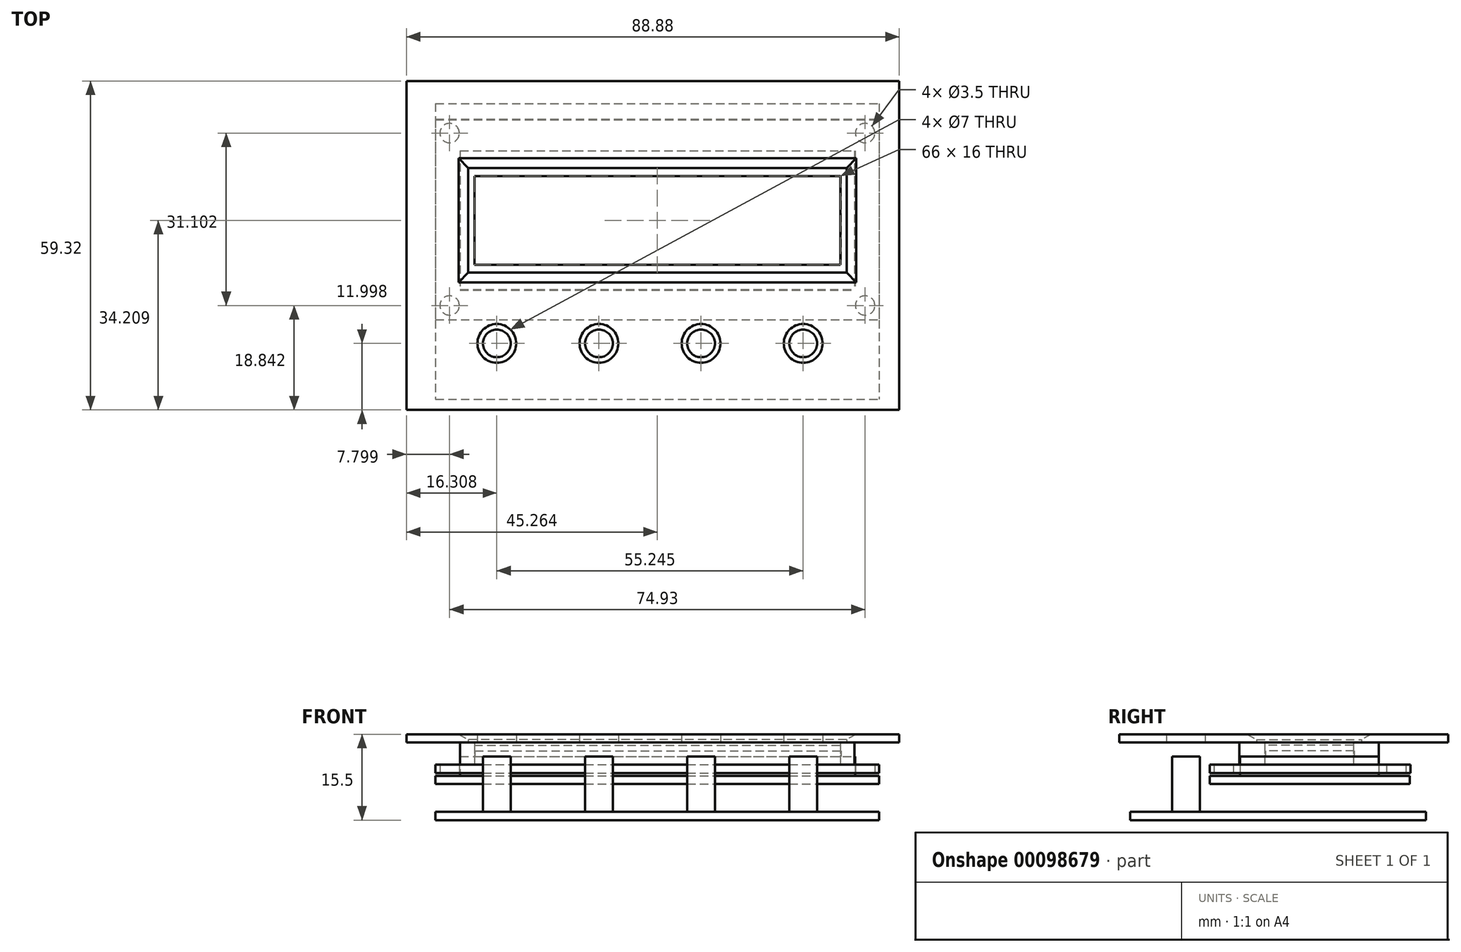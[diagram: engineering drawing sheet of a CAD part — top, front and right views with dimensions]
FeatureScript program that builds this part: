
annotation { "Feature Type Name" : "Feature", "Feature Type Description" : "" }
export const myFeature = defineFeature(function(context is Context, id is Id, definition is map)
    precondition{}
    {
        {
            var Q0;
            Q0=qCreatedBy(makeId("Top.planeOp"),FACE);
            var sketch = newSketch(context, id + "F0", { "sketchPlane" : qUnion([Q0])});
            skLineSegment(sketch, "E0.bottom", {"start": v(-57.33, 22.05) * mm, "end": v(22.68, 22.05) * mm});
            skLineSegment(sketch, "E0.top", {"start": v(-57.33, -31.29) * mm, "end": v(22.68, -31.29) * mm});
            skLineSegment(sketch, "E0.left", {"start": v(-57.33, 22.05) * mm, "end": v(-57.33, -31.29) * mm});
            skLineSegment(sketch, "E0.right", {"start": v(22.68, 22.05) * mm, "end": v(22.68, -31.29) * mm});
            skCircle(sketch, "E1", {"center": v(-46.28, -21.24) * mm, "radius": 2.5 * mm});
            skCircle(sketch, "E2", {"center": v(-27.87, -21.24) * mm, "radius": 2.5 * mm});
            skCircle(sketch, "E3", {"center": v(8.96, -21.24) * mm, "radius": 2.5 * mm});
            skCircle(sketch, "E4", {"center": v(-9.45, -21.24) * mm, "radius": 2.5 * mm});
            skLineSegment(sketch, "E5", {"start": v(-57.33, -16.94) * mm, "end": v(22.68, -16.94) * mm});
            skLineSegment(sketch, "E6", {"start": v(-57.33, 19.13) * mm, "end": v(22.68, 19.13) * mm});
            skLineSegment(sketch, "E7.bottom", {"start": v(-52.89, 13.54) * mm, "end": v(18.36, 13.54) * mm});
            skLineSegment(sketch, "E7.top", {"start": v(-52.89, -11.48) * mm, "end": v(18.36, -11.48) * mm});
            skLineSegment(sketch, "E7.left", {"start": v(-52.89, 13.54) * mm, "end": v(-52.89, -11.48) * mm});
            skLineSegment(sketch, "E7.right", {"start": v(18.36, 13.54) * mm, "end": v(18.36, -11.48) * mm});
            skLineSegment(sketch, "E8.bottom", {"start": v(-50.22, 9.1) * mm, "end": v(15.82, 9.1) * mm});
            skLineSegment(sketch, "E8.top", {"start": v(-50.22, -6.9) * mm, "end": v(15.82, -6.9) * mm});
            skLineSegment(sketch, "E8.left", {"start": v(-50.22, 9.1) * mm, "end": v(-50.22, -6.9) * mm});
            skLineSegment(sketch, "E8.right", {"start": v(15.82, 9.1) * mm, "end": v(15.82, -6.9) * mm});
            skSolve(sketch);
        }
        {
            var Q0;
            {var subQ1=sQuery(id+"F0.wireOp",EDGE,"E5");Q0=makeQuery(id+"F0.imprint","IMPRINT",FACE,{"disambiguationData":[TD([[makeQuery(id+"F0.imprint","IMPRINT",EDGE,{"derivedFrom":subQ1}),1.0]])]});}
            var Q1;
            Q1=makeQuery(id+"F0.imprint","IMPRINT",FACE,{"disambiguationData":[TD([[makeQuery(id+"F0.imprint","IMPRINT",EDGE,{"derivedFrom":sQuery(id+"F0.wireOp",EDGE,"E8.bottom")}),-1.0]])]});
            var Q2;
            {var subQ0=sQuery(id+"F0.wireOp",EDGE,"E0.bottom");Q2=makeQuery(id+"F0.imprint","IMPRINT",FACE,{"disambiguationData":[TD([[makeQuery(id+"F0.imprint","IMPRINT",EDGE,{"derivedFrom":subQ0}),-1.0]])]});}
            var Q3;
            Q3=makeQuery(id+"F0.imprint","IMPRINT",FACE,{"disambiguationData":[TD([[makeQuery(id+"F0.imprint","IMPRINT",EDGE,{"derivedFrom":sQuery(id+"F0.wireOp",EDGE,"E4")}),1.0]])]});
            var Q4;
            Q4=makeQuery(id+"F0.imprint","IMPRINT",FACE,{"disambiguationData":[TD([[makeQuery(id+"F0.imprint","IMPRINT",EDGE,{"derivedFrom":sQuery(id+"F0.wireOp",EDGE,"E7.bottom")}),-1.0]])]});
            var Q5;
            Q5=makeQuery(id+"F0.imprint","IMPRINT",FACE,{"disambiguationData":[TD([[makeQuery(id+"F0.imprint","IMPRINT",EDGE,{"derivedFrom":sQuery(id+"F0.wireOp",EDGE,"E1")}),1.0]])]});
            var Q6;
            Q6=makeQuery(id+"F0.imprint","IMPRINT",FACE,{"disambiguationData":[TD([[makeQuery(id+"F0.imprint","IMPRINT",EDGE,{"derivedFrom":sQuery(id+"F0.wireOp",EDGE,"E2")}),1.0]])]});
            var Q7;
            Q7=makeQuery(id+"F0.imprint","IMPRINT",FACE,{"disambiguationData":[TD([[makeQuery(id+"F0.imprint","IMPRINT",EDGE,{"derivedFrom":sQuery(id+"F0.wireOp",EDGE,"E3")}),1.0]])]});
            var Q8;
            {var subQ0=sQuery(id+"F0.wireOp",EDGE,"E0.top");Q8=makeQuery(id+"F0.imprint","IMPRINT",FACE,{"disambiguationData":[TD([[makeQuery(id+"F0.imprint","IMPRINT",EDGE,{"derivedFrom":subQ0}),1.0]])]});}
            extrude(context, id + "F1", {"entities" : qUnion([Q0, Q1, Q2, Q3, Q4, Q5, Q6, Q7, Q8]), "oppositeDirection" : true, "depth" : 1.5 * mm});
        }
        {
            var Q0;
            Q0=makeQuery(id+"F0.imprint","IMPRINT",FACE,{"disambiguationData":[TD([[makeQuery(id+"F0.imprint","IMPRINT",EDGE,{"derivedFrom":sQuery(id+"F0.wireOp",EDGE,"E1")}),1.0]])]});
            var Q1;
            Q1=makeQuery(id+"F0.imprint","IMPRINT",FACE,{"disambiguationData":[TD([[makeQuery(id+"F0.imprint","IMPRINT",EDGE,{"derivedFrom":sQuery(id+"F0.wireOp",EDGE,"E2")}),1.0]])]});
            var Q2;
            Q2=makeQuery(id+"F0.imprint","IMPRINT",FACE,{"disambiguationData":[TD([[makeQuery(id+"F0.imprint","IMPRINT",EDGE,{"derivedFrom":sQuery(id+"F0.wireOp",EDGE,"E4")}),1.0]])]});
            var Q3;
            Q3=makeQuery(id+"F0.imprint","IMPRINT",FACE,{"disambiguationData":[TD([[makeQuery(id+"F0.imprint","IMPRINT",EDGE,{"derivedFrom":sQuery(id+"F0.wireOp",EDGE,"E3")}),1.0]])]});
            extrude(context, id + "F2", {"entities" : qUnion([Q0, Q1, Q2, Q3]), "depth" : 10 * mm});
        }
        {
            var Q0;
            Q0=makeQuery(id+"F1.opExtrude","CAP_FACE",FACE,{"disambiguationData":[OSD([sQuery(id+"F0.wireOp",EDGE,"E0.bottom"),sQuery(id+"F0.wireOp",EDGE,"E0.top"),sQuery(id+"F0.wireOp",EDGE,"E0.left"),sQuery(id+"F0.wireOp",EDGE,"E0.right")])],"isStart":true});
            cPlane(context, id + "F3", {"entities" : qUnion([Q0]), "cplaneType" : CPlaneType.OFFSET, "offset" : 7 * mm, "width" : 150 * mm, "height" : 150 * mm});
        }
        {
            var Q0;
            Q0=qCreatedBy(id+"F3.planeOp",FACE);
            var sketch = newSketch(context, id + "F4", { "sketchPlane" : qUnion([Q0])});
            skLineSegment(sketch, "E9.0", {"start": v(-57.33, 22.05) * mm, "end": v(-57.33, -31.29) * mm, "construction": true});
            skLineSegment(sketch, "E10.0", {"start": v(-57.33, -31.29) * mm, "end": v(22.68, -31.29) * mm, "construction": true});
            skLineSegment(sketch, "E11.bottom", {"start": v(-57.33, 19.24) * mm, "end": v(22.68, 19.24) * mm});
            skLineSegment(sketch, "E11.top", {"start": v(-57.33, -16.94) * mm, "end": v(22.68, -16.94) * mm});
            skLineSegment(sketch, "E11.left", {"start": v(-57.33, 19.24) * mm, "end": v(-57.33, -16.94) * mm});
            skLineSegment(sketch, "E11.right", {"start": v(22.68, 19.24) * mm, "end": v(22.68, -16.94) * mm});
            skCircle(sketch, "E12", {"center": v(-54.8, -14.4) * mm, "radius": 1.75 * mm});
            skCircle(sketch, "E13", {"center": v(-54.8, 16.7) * mm, "radius": 1.75 * mm});
            skCircle(sketch, "E14", {"center": v(20.14, 16.7) * mm, "radius": 1.75 * mm});
            skCircle(sketch, "E15", {"center": v(20.14, -14.4) * mm, "radius": 1.75 * mm});
            skSolve(sketch);
        }
        {
            var Q0;
            Q0 = qSketchRegion(id + "F4", true);
            extrude(context, id + "F5", {"entities" : qUnion([Q0]), "depth" : 1.5 * mm});
        }
        {
            var Q0;
            Q0=makeQuery(id+"F5.opExtrude","CAP_FACE",FACE,{"disambiguationData":[OSD([sQuery(id+"F4.wireOp",EDGE,"E11.bottom"),sQuery(id+"F4.wireOp",EDGE,"E11.top"),sQuery(id+"F4.wireOp",EDGE,"E11.left"),sQuery(id+"F4.wireOp",EDGE,"E11.right"),sQuery(id+"F4.wireOp",EDGE,"E12"),sQuery(id+"F4.wireOp",EDGE,"E13"),sQuery(id+"F4.wireOp",EDGE,"E14"),sQuery(id+"F4.wireOp",EDGE,"E15"),sQuery(id+"F4.wireOp",EDGE,"9yUqGMXj-hSxB-kQKk-yNBa-DG6KZY831I2t")])],"isStart":false});
            var sketch = newSketch(context, id + "F6", { "sketchPlane" : qUnion([Q0])});
            skLineSegment(sketch, "E16.bottom", {"start": v(-52.89, 13.54) * mm, "end": v(18.23, 13.54) * mm});
            skLineSegment(sketch, "E16.top", {"start": v(-52.89, -11.6) * mm, "end": v(18.23, -11.6) * mm});
            skLineSegment(sketch, "E16.left", {"start": v(-52.89, 13.54) * mm, "end": v(-52.89, -11.6) * mm});
            skLineSegment(sketch, "E16.right", {"start": v(18.23, 13.54) * mm, "end": v(18.23, -11.6) * mm});
            skLineSegment(sketch, "E17.0", {"start": v(-57.33, 19.24) * mm, "end": v(22.68, 19.24) * mm});
            skLineSegment(sketch, "E18", {"start": v(-17.33, 19.24) * mm, "end": v(-17.33, -16.94) * mm, "construction": true});
            skLineSegment(sketch, "E19.bottom", {"start": v(-50.33, 8.97) * mm, "end": v(15.67, 8.97) * mm});
            skLineSegment(sketch, "E19.top", {"start": v(-50.33, -7.03) * mm, "end": v(15.67, -7.03) * mm});
            skLineSegment(sketch, "E19.left", {"start": v(-50.33, 8.97) * mm, "end": v(-50.33, -7.03) * mm});
            skLineSegment(sketch, "E19.right", {"start": v(15.67, 8.97) * mm, "end": v(15.67, -7.03) * mm});
            skLineSegment(sketch, "E20", {"start": v(-52.89, 0.97) * mm, "end": v(18.23, 0.97) * mm, "construction": true});
            skSolve(sketch);
        }
        {
            var Q0;
            Q0=makeQuery(id+"F6.imprint","IMPRINT",FACE,{"disambiguationData":[TD([[makeQuery(id+"F6.imprint","IMPRINT",EDGE,{"derivedFrom":sQuery(id+"F6.wireOp",EDGE,"E16.bottom")}),-1.0]])]});
            extrude(context, id + "F7", {"entities" : qUnion([Q0]), "depth" : 4 * mm});
        }
        {
            var Q0;
            Q0=makeQuery(id+"F6.imprint","IMPRINT",FACE,{"disambiguationData":[TD([[makeQuery(id+"F6.imprint","IMPRINT",EDGE,{"derivedFrom":sQuery(id+"F6.wireOp",EDGE,"E19.bottom")}),-1.0]])]});
            extrude(context, id + "F8", {"entities" : qUnion([Q0]), "depth" : 3.5 * mm});
        }
        {
            var Q0;
            Q0=makeQuery(id+"F7.opExtrude","CAP_FACE",FACE,{"disambiguationData":[OSD([sQuery(id+"F6.wireOp",EDGE,"E16.bottom"),sQuery(id+"F6.wireOp",EDGE,"E16.top"),sQuery(id+"F6.wireOp",EDGE,"E16.left"),sQuery(id+"F6.wireOp",EDGE,"E16.right"),sQuery(id+"F6.wireOp",EDGE,"E19.bottom"),sQuery(id+"F6.wireOp",EDGE,"E19.top"),sQuery(id+"F6.wireOp",EDGE,"E19.left"),sQuery(id+"F6.wireOp",EDGE,"E19.right")])],"isStart":false});
            var sketch = newSketch(context, id + "F9", { "sketchPlane" : qUnion([Q0])});
            skLineSegment(sketch, "E21.0", {"start": v(-57.33, -31.29) * mm, "end": v(22.68, -31.29) * mm, "construction": true});
            skCircle(sketch, "E22.0", {"center": v(-46.28, -21.24) * mm, "radius": 2.5 * mm, "construction": true});
            skCircle(sketch, "E23.0", {"center": v(-27.87, -21.24) * mm, "radius": 2.5 * mm, "construction": true});
            skCircle(sketch, "E24.0", {"center": v(-9.45, -21.24) * mm, "radius": 2.5 * mm, "construction": true});
            skCircle(sketch, "E25.0", {"center": v(8.96, -21.24) * mm, "radius": 2.5 * mm, "construction": true});
            skLineSegment(sketch, "E26", {"start": v(-52.89, 0.97) * mm, "end": v(18.23, 0.97) * mm, "construction": true});
            skLineSegment(sketch, "E27.0", {"start": v(16.78, 10.43) * mm, "end": v(-51.43, 10.43) * mm});
            skLineSegment(sketch, "E27.1", {"start": v(16.78, -8.49) * mm, "end": v(16.78, 10.43) * mm});
            skLineSegment(sketch, "E27.2", {"start": v(-51.43, -8.49) * mm, "end": v(16.78, -8.49) * mm});
            skLineSegment(sketch, "E27.3", {"start": v(-51.43, 10.43) * mm, "end": v(-51.43, -8.49) * mm});
            skLineSegment(sketch, "E28.bottom", {"start": v(-62.6, 26.08) * mm, "end": v(26.29, 26.08) * mm});
            skLineSegment(sketch, "E28.top", {"start": v(-62.6, -33.24) * mm, "end": v(26.29, -33.24) * mm});
            skLineSegment(sketch, "E28.left", {"start": v(-62.6, 26.08) * mm, "end": v(-62.6, -33.24) * mm});
            skLineSegment(sketch, "E28.right", {"start": v(26.29, 26.08) * mm, "end": v(26.29, -33.24) * mm});
            skCircle(sketch, "E29.0", {"center": v(-46.28, -21.24) * mm, "radius": 3.5 * mm});
            skCircle(sketch, "E30", {"center": v(-27.87, -21.24) * mm, "radius": 3.5 * mm});
            skCircle(sketch, "E31", {"center": v(-9.45, -21.24) * mm, "radius": 3.5 * mm});
            skCircle(sketch, "E32", {"center": v(8.96, -21.24) * mm, "radius": 3.5 * mm});
            skLineSegment(sketch, "E33", {"start": v(-17.33, 13.54) * mm, "end": v(-17.33, -11.6) * mm, "construction": true});
            skSolve(sketch);
        }
        {
            var Q0;
            Q0=makeQuery(id+"F9.imprint","IMPRINT",FACE,{"disambiguationData":[TD([[makeQuery(id+"F9.imprint","IMPRINT",EDGE,{"derivedFrom":sQuery(id+"F9.wireOp",EDGE,"E28.bottom")}),-1.0]])]});
            var Q1;
            Q1=makeQuery(id+"F9.imprint","IMPRINT",FACE,{"disambiguationData":[TD([[makeQuery(id+"F9.imprint","IMPRINT",EDGE,{"derivedFrom":sQuery(id+"F9.wireOp",EDGE,"E27.0")}),-1.0]])]});
            extrude(context, id + "F10", {"entities" : qUnion([Q0, Q1]), "depth" : 1.5 * mm});
        }
        {
            var Q0;
            Q0=makeQuery(id+"F10.opExtrude","CAP_EDGE",EDGE,{"disambiguationData":[OSD([sQuery(id+"F9.wireOp",EDGE,"E27.0")])],"isStart":false});
            var Q1;
            Q1=makeQuery(id+"F10.opExtrude","CAP_EDGE",EDGE,{"disambiguationData":[OSD([sQuery(id+"F9.wireOp",EDGE,"E27.3")])],"isStart":false});
            var Q2;
            Q2=makeQuery(id+"F10.opExtrude","CAP_EDGE",EDGE,{"disambiguationData":[OSD([sQuery(id+"F9.wireOp",EDGE,"E27.2")])],"isStart":false});
            var Q3;
            Q3=makeQuery(id+"F10.opExtrude","CAP_EDGE",EDGE,{"disambiguationData":[OSD([sQuery(id+"F9.wireOp",EDGE,"E27.1")])],"isStart":false});
            chamfer(context, id + "F11", {"entities" : qUnion([Q0, Q1, Q2, Q3]), "chamferType" : ChamferType.OFFSET_ANGLE, "width" : 1 * mm, "oppositeDirection" : false, "angle" : 60 * degree, "tangentPropagation" : true});
        }
        {
            var Q0;
            Q0=makeQuery(id+"F0.imprint","IMPRINT",FACE,{"disambiguationData":[TD([[makeQuery(id+"F0.imprint","IMPRINT",EDGE,{"derivedFrom":sQuery(id+"F0.wireOp",EDGE,"E7.bottom")}),-1.0]])]});
            var Q1;
            Q1=makeQuery(id+"F0.imprint","IMPRINT",FACE,{"disambiguationData":[TD([[makeQuery(id+"F0.imprint","IMPRINT",EDGE,{"derivedFrom":sQuery(id+"F0.wireOp",EDGE,"E8.bottom")}),-1.0]])]});
            var Q2;
            {var subQ1=sQuery(id+"F0.wireOp",EDGE,"E5");Q2=makeQuery(id+"F0.imprint","IMPRINT",FACE,{"disambiguationData":[TD([[makeQuery(id+"F0.imprint","IMPRINT",EDGE,{"derivedFrom":subQ1}),1.0]])]});}
            extrude(context, id + "F12", {"entities" : qUnion([Q0, Q1, Q2]), "depth" : 6.5 * mm, "hasSecondDirection" : true, "secondDirectionOppositeDirection" : false, "secondDirectionDepth" : 5 * mm});
        }
        {
            var Q0;
            Q0=makeQuery(id+"F0.imprint","IMPRINT",FACE,{"disambiguationData":[TD([[makeQuery(id+"F0.imprint","IMPRINT",EDGE,{"derivedFrom":sQuery(id+"F0.wireOp",EDGE,"E8.bottom")}),-1.0]])]});
            var Q1;
            Q1=makeQuery(id+"F0.imprint","IMPRINT",FACE,{"disambiguationData":[TD([[makeQuery(id+"F0.imprint","IMPRINT",EDGE,{"derivedFrom":sQuery(id+"F0.wireOp",EDGE,"E7.bottom")}),-1.0]])]});
            extrude(context, id + "F13", {"entities" : qUnion([Q0, Q1]), "depth" : 10 * mm, "hasSecondDirection" : true, "secondDirectionOppositeDirection" : false, "secondDirectionDepth" : 6.5 * mm});
        }
        {
            var Q0;
            Q0=makeQuery(id+"F0.imprint","IMPRINT",FACE,{"disambiguationData":[TD([[makeQuery(id+"F0.imprint","IMPRINT",EDGE,{"derivedFrom":sQuery(id+"F0.wireOp",EDGE,"E8.bottom")}),-1.0]])]});
            extrude(context, id + "F14", {"entities" : qUnion([Q0]), "depth" : 11 * mm, "hasSecondDirection" : true, "secondDirectionOppositeDirection" : false, "secondDirectionDepth" : 10 * mm});
        }
    });
